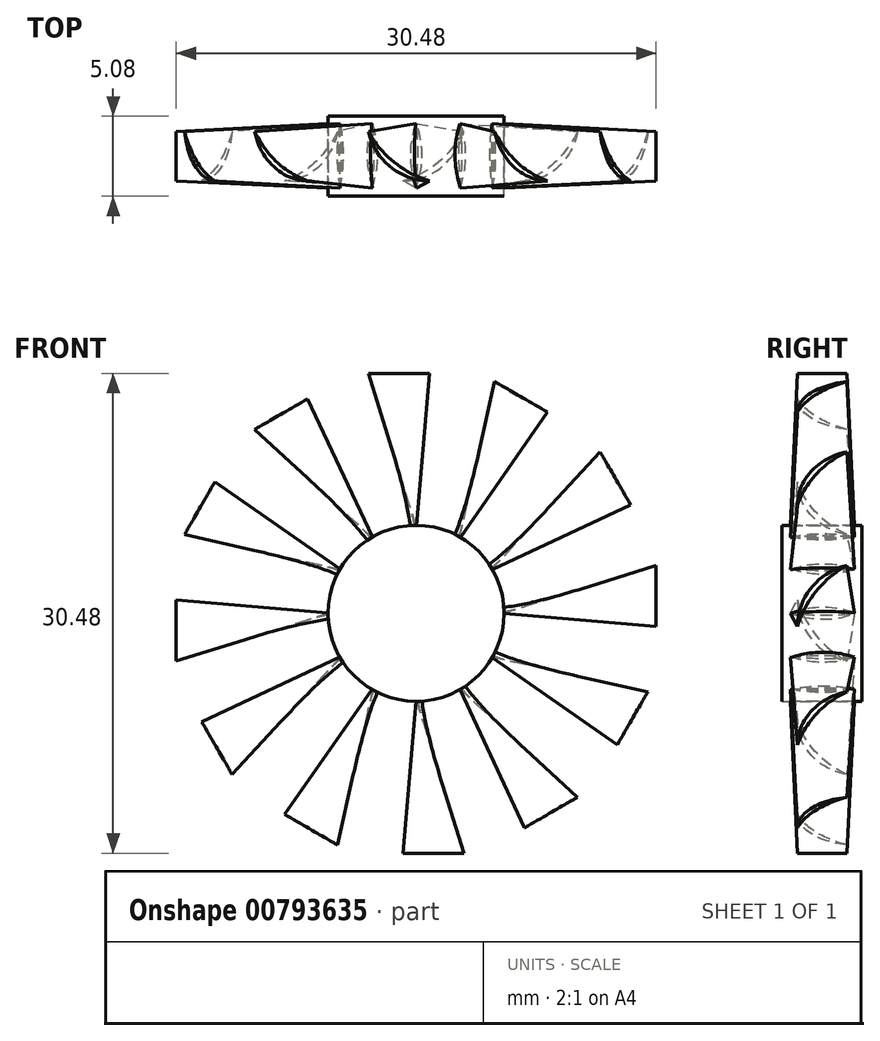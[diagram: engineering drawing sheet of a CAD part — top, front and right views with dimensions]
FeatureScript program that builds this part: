
annotation { "Feature Type Name" : "Feature", "Feature Type Description" : "" }
export const myFeature = defineFeature(function(context is Context, id is Id, definition is map)
    precondition{}
    {
        {
            var Q0;
            Q0=qCreatedBy(makeId("Front.planeOp"),FACE);
            var sketch = newSketch(context, id + "F0", { "sketchPlane" : qUnion([Q0])});
            skCircle(sketch, "E0", {"center": v(0, 0) * mm, "radius": 5.59 * mm});
            skSolve(sketch);
        }
        {
            var Q0;
            Q0 = qSketchRegion(id + "F0", true);
            extrude(context, id + "F1", {"entities" : qUnion([Q0]), "depth" : 5.08 * mm, "offsetDistance" : 25.4 * mm});
        }
        {
            var Q0;
            Q0=qCreatedBy(makeId("Right.planeOp"),FACE);
            cPlane(context, id + "F2", {"entities" : qUnion([Q0]), "cplaneType" : CPlaneType.OFFSET, "offset" : 15.24 * mm, "width" : 152.4 * mm, "height" : 152.4 * mm});
        }
        {
            var Q0;
            Q0=qCreatedBy(makeId("Right.planeOp"),FACE);
            cPlane(context, id + "F3", {"entities" : qUnion([Q0]), "cplaneType" : CPlaneType.OFFSET, "offset" : 5.6 * mm, "width" : 152.4 * mm, "height" : 152.4 * mm});
        }
        {
            var Q0;
            Q0=qCreatedBy(id+"F3.planeOp",FACE);
            var sketch = newSketch(context, id + "F4", { "sketchPlane" : qUnion([Q0])});
            skArc(sketch, "E1", {"start": v(-0.48, 0.02) * mm, "mid": v(-2.52, 0.37) * mm, "end": v(-4.55, -0.02) * mm});
            skArc(sketch, "E2", {"start": v(-0.48, 0.02) * mm, "mid": v(-2.51, 0.11) * mm, "end": v(-4.55, -0.02) * mm});
            skSolve(sketch);
        }
        {
            var Q0;
            Q0=qCreatedBy(id+"F2.planeOp",FACE);
            var sketch = newSketch(context, id + "F5", { "sketchPlane" : qUnion([Q0])});
            skArc(sketch, "E3", {"start": v(-0.96, 3.04) * mm, "mid": v(-3.2, 1.64) * mm, "end": v(-4.1, -0.84) * mm});
            skArc(sketch, "E4", {"start": v(-0.96, 3.04) * mm, "mid": v(-2.91, 1.4) * mm, "end": v(-4.1, -0.84) * mm});
            skSolve(sketch);
        }
        {
            var Q0;
            Q0=makeQuery(id+"F4.imprint","IMPRINT",FACE,{"disambiguationData":[TD([[makeQuery(id+"F4.imprint","IMPRINT",EDGE,{"derivedFrom":sQuery(id+"F4.wireOp",EDGE,"E1")}),1.0]])]});
            var Q1;
            Q1=makeQuery(id+"F5.imprint","IMPRINT",FACE,{"disambiguationData":[TD([[makeQuery(id+"F5.imprint","IMPRINT",EDGE,{"derivedFrom":sQuery(id+"F5.wireOp",EDGE,"E3")}),1.0]])]});
            loft(context, id + "F6", {"sheetProfilesArray" : [{ "sheetProfileEntities" : qUnion([Q0]) }, { "sheetProfileEntities" : qUnion([Q1]) }]});
        }
        {
            var Q0;
            Q0=makeQuery(id+"F6.opLoft","SWEPT_BODY",BODY,{"disambiguationData":[OSD([makeQuery(id+"F4.imprint","IMPRINT",FACE,{"disambiguationData":[TD([[makeQuery(id+"F4.imprint","IMPRINT",EDGE,{"derivedFrom":sQuery(id+"F4.wireOp",EDGE,"E1")}),1.0]])]}),makeQuery(id+"F5.imprint","IMPRINT",FACE,{"disambiguationData":[TD([[makeQuery(id+"F5.imprint","IMPRINT",EDGE,{"derivedFrom":sQuery(id+"F5.wireOp",EDGE,"E3")}),1.0]])]})])]});
            var Q1;
            Q1=makeQuery(id+"F1.opExtrude","CAP_EDGE",EDGE,{"disambiguationData":[OSD([sQuery(id+"F0.wireOp",EDGE,"E0")])],"isStart":true});
            circularPattern(context, id + "F7", {"entities" : qUnion([Q0]), "axis" : qUnion([Q1]), "angle" : 360 * degree, "instanceCount" : 12, "equalSpace" : true});
        }
    });
